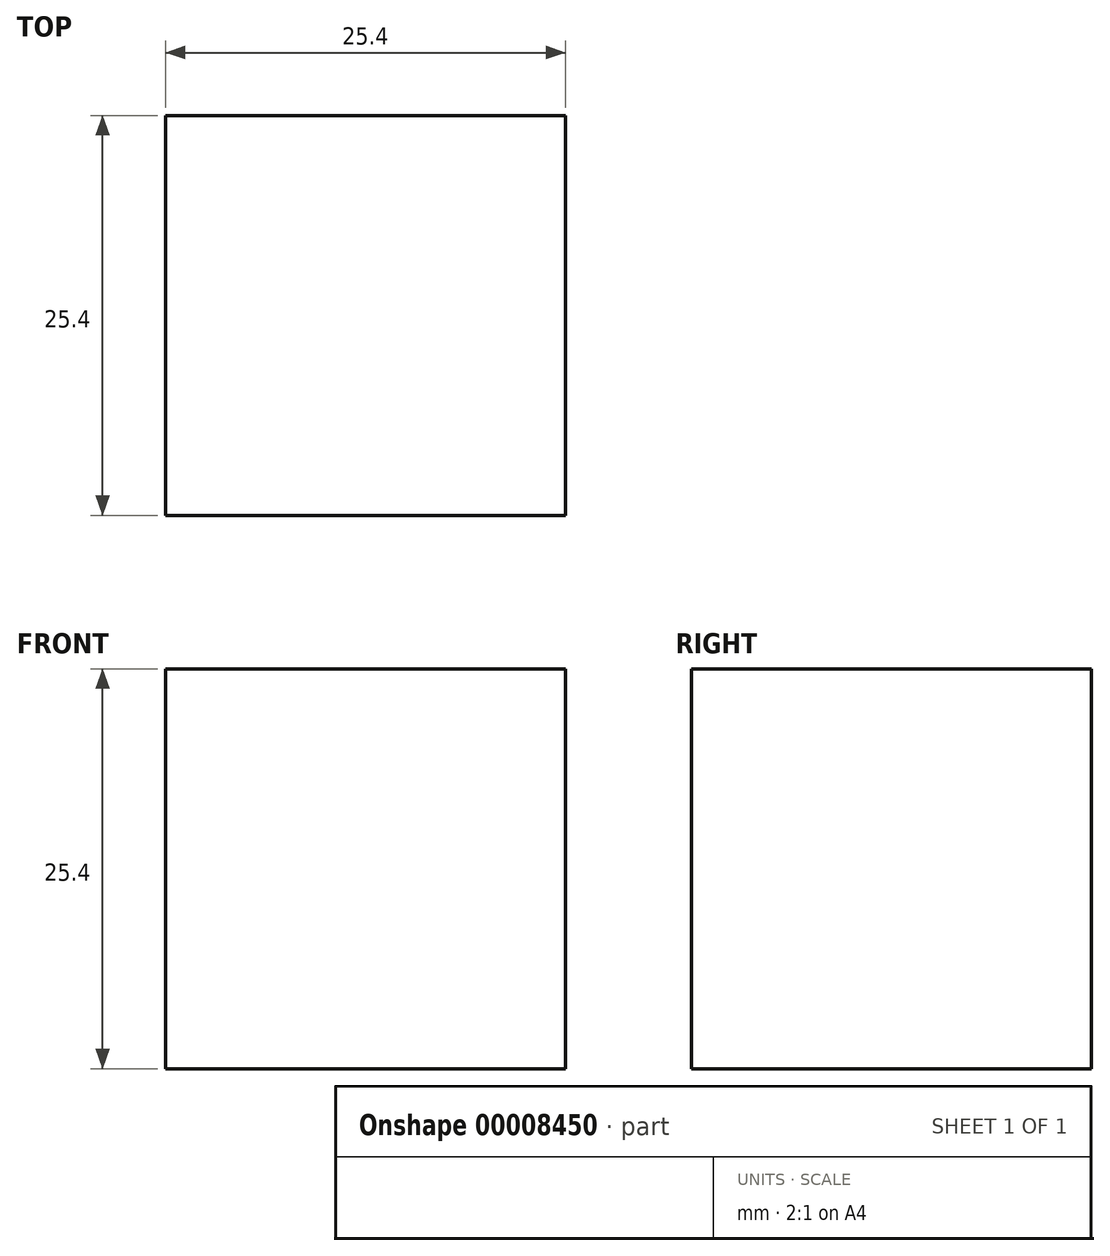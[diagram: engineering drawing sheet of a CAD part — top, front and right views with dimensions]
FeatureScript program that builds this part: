
annotation { "Feature Type Name" : "Feature", "Feature Type Description" : "" }
export const myFeature = defineFeature(function(context is Context, id is Id, definition is map)
    precondition{}
    {
        {
            var Q0;
            Q0=qCreatedBy(makeId("Top.planeOp"),FACE);
            var sketch = newSketch(context, id + "F0", { "sketchPlane" : qUnion([Q0])});
            skLineSegment(sketch, "E0.bottom", {"start": v(-36.84, 24.1) * mm, "end": v(-11.44, 24.1) * mm});
            skLineSegment(sketch, "E0.top", {"start": v(-36.84, -1.3) * mm, "end": v(-11.44, -1.3) * mm});
            skLineSegment(sketch, "E0.left", {"start": v(-36.84, 24.1) * mm, "end": v(-36.84, -1.3) * mm});
            skLineSegment(sketch, "E0.right", {"start": v(-11.44, 24.1) * mm, "end": v(-11.44, -1.3) * mm});
            skSolve(sketch);
        }
        {
            var Q0;
            Q0=makeQuery(id+"F0.imprint","IMPRINT",FACE,{"disambiguationData":[TD([[makeQuery(id+"F0.imprint","IMPRINT",EDGE,{"derivedFrom":sQuery(id+"F0.wireOp",EDGE,"E0.bottom")}),-1.0]])]});
            extrude(context, id + "F1", {"entities" : qUnion([Q0]), "depth" : 25.4 * mm});
        }
    });
